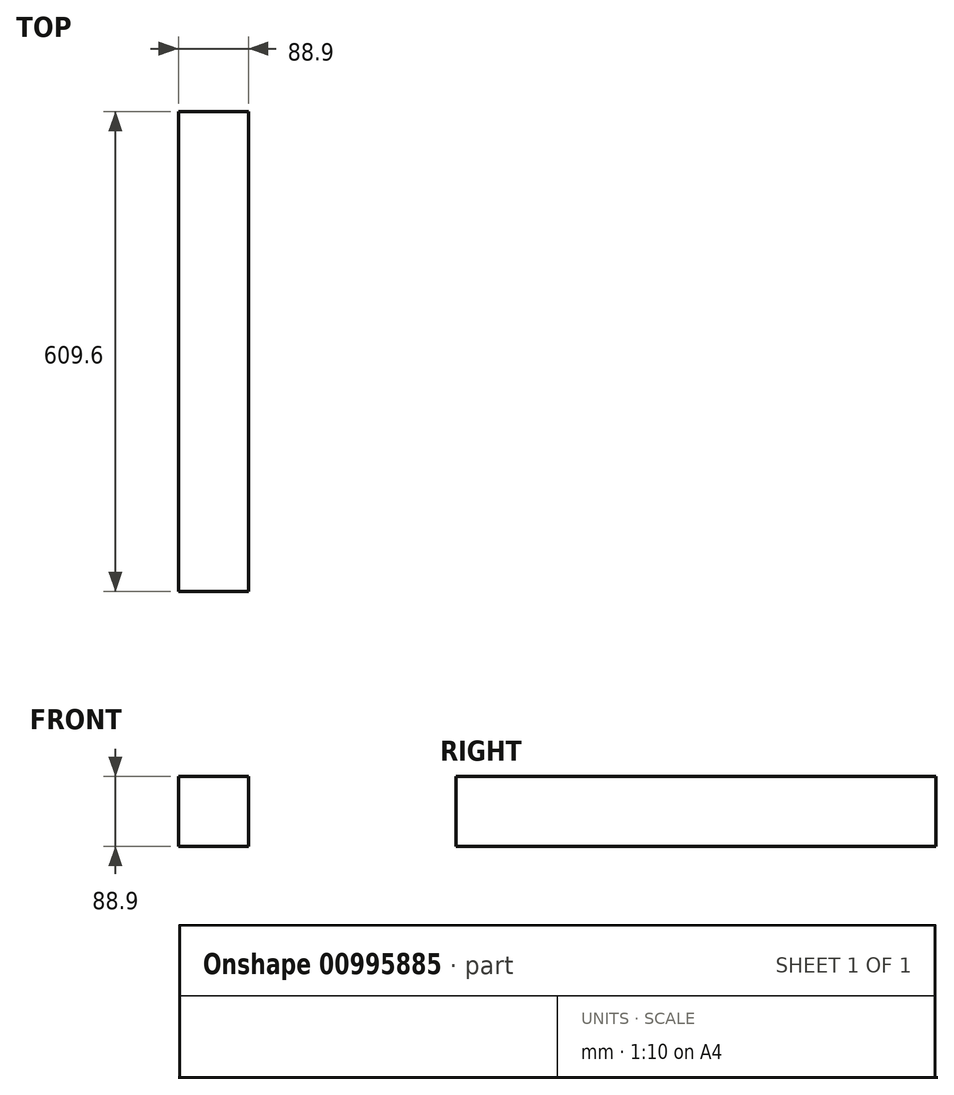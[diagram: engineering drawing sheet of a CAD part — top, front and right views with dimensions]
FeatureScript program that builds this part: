
annotation { "Feature Type Name" : "Feature", "Feature Type Description" : "" }
export const myFeature = defineFeature(function(context is Context, id is Id, definition is map)
    precondition{}
    {
        {
            var Q0;
            Q0=qCreatedBy(makeId("Front.planeOp"),FACE);
            var sketch = newSketch(context, id + "F0", { "sketchPlane" : qUnion([Q0])});
            skLineSegment(sketch, "E0.bottom", {"start": v(0, 0) * mm, "end": v(88.9, 0) * mm});
            skLineSegment(sketch, "E0.top", {"start": v(0, 88.9) * mm, "end": v(88.9, 88.9) * mm});
            skLineSegment(sketch, "E0.left", {"start": v(0, 0) * mm, "end": v(0, 88.9) * mm});
            skLineSegment(sketch, "E0.right", {"start": v(88.9, 0) * mm, "end": v(88.9, 88.9) * mm});
            skSolve(sketch);
        }
        {
            var Q0;
            Q0 = qSketchRegion(id + "F0", true);
            extrude(context, id + "F1", {"entities" : qUnion([Q0]), "depth" : 609.6 * mm, "offsetDistance" : 25.4 * mm});
        }
    });
